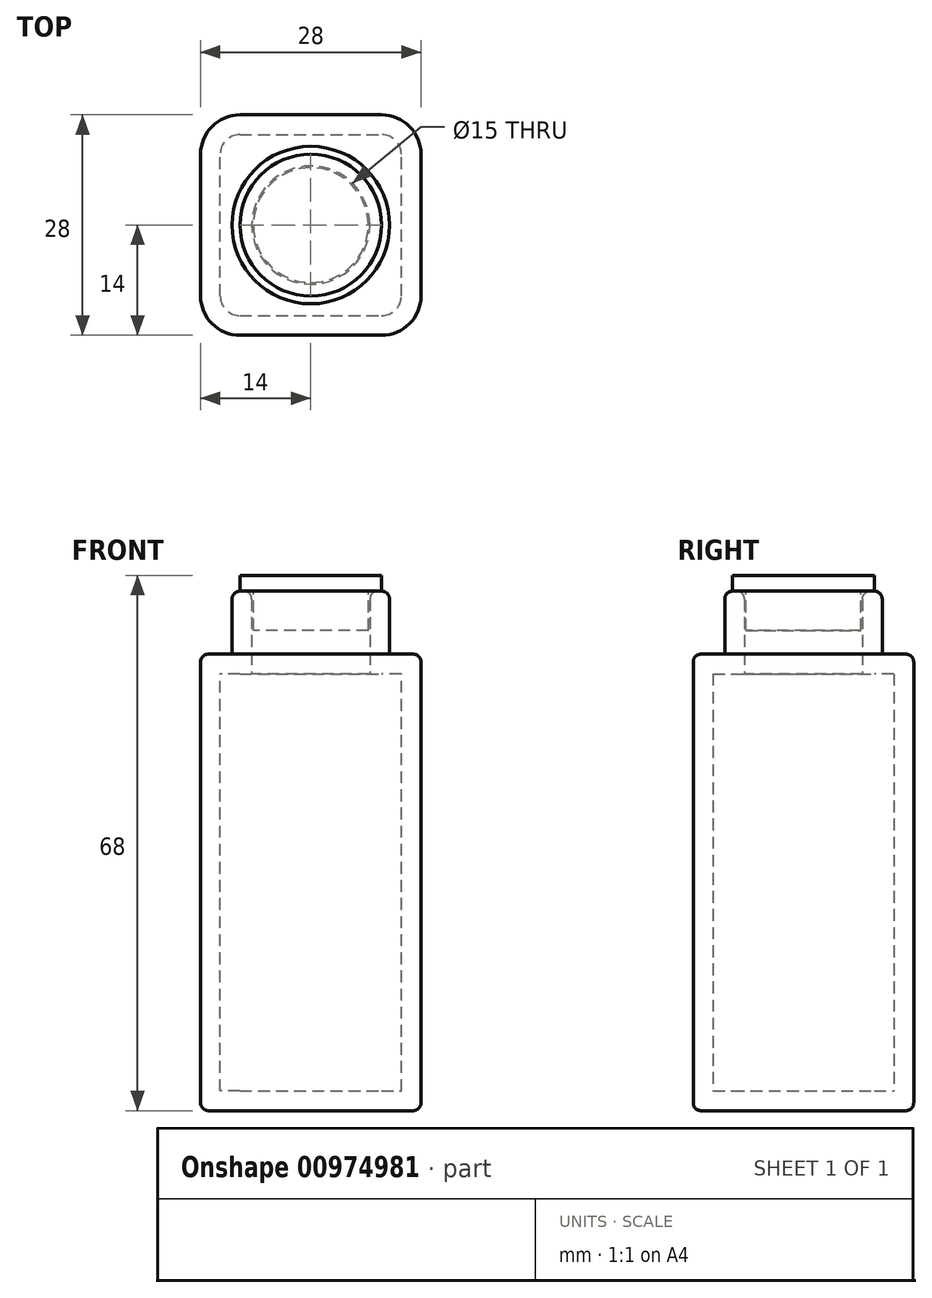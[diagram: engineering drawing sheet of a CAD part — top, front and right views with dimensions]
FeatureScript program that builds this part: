
annotation { "Feature Type Name" : "Feature", "Feature Type Description" : "" }
export const myFeature = defineFeature(function(context is Context, id is Id, definition is map)
    precondition{}
    {
        {
            var Q0;
            Q0=qCreatedBy(makeId("Top.planeOp"),FACE);
            var sketch = newSketch(context, id + "F0", { "sketchPlane" : qUnion([Q0])});
            skLineSegment(sketch, "E0.bottom", {"start": v(14, -14) * mm, "end": v(-14, -14) * mm});
            skLineSegment(sketch, "E0.top", {"start": v(14, 14) * mm, "end": v(-14, 14) * mm});
            skLineSegment(sketch, "E0.left", {"start": v(14, -14) * mm, "end": v(14, 14) * mm});
            skLineSegment(sketch, "E0.right", {"start": v(-14, -14) * mm, "end": v(-14, 14) * mm});
            skPoint(sketch, "E0.middle", {"position": v(0, 0) * mm});
            skSolve(sketch);
        }
        {
            var Q0;
            Q0=makeQuery(id+"F0.imprint","IMPRINT",FACE,{"disambiguationData":[TD([[makeQuery(id+"F0.imprint","IMPRINT",EDGE,{"derivedFrom":sQuery(id+"F0.wireOp",EDGE,"E0.bottom")}),-1.0]])]});
            extrude(context, id + "F1", {"entities" : qUnion([Q0]), "depth" : 58 * mm, "offsetDistance" : 25 * mm});
        }
        {
            var Q0;
            Q0=makeQuery(id+"F1.opExtrude","CAP_FACE",FACE,{"disambiguationData":[OSD([sQuery(id+"F0.wireOp",EDGE,"E0.bottom"),sQuery(id+"F0.wireOp",EDGE,"E0.top"),sQuery(id+"F0.wireOp",EDGE,"E0.left"),sQuery(id+"F0.wireOp",EDGE,"E0.right")])],"isStart":false});
            var sketch = newSketch(context, id + "F2", { "sketchPlane" : qUnion([Q0])});
            skCircle(sketch, "E1", {"center": v(0, 0) * mm, "radius": 10 * mm});
            skSolve(sketch);
        }
        {
            var Q0;
            Q0=makeQuery(id+"F2.imprint","IMPRINT",FACE,{"disambiguationData":[TD([[makeQuery(id+"F2.imprint","IMPRINT",EDGE,{"derivedFrom":sQuery(id+"F2.wireOp",EDGE,"E1")}),1.0]])]});
            extrude(context, id + "F3", {"entities" : qUnion([Q0]), "operationType" : NewBodyOperationType.ADD, "depth" : 8 * mm, "offsetDistance" : 25 * mm});
        }
        {
            var Q0;
            Q0=makeQuery(id+"F1.opExtrude","SWEPT_EDGE",EDGE,{"disambiguationData":[OSD([sQuery(id+"F0.wireOp",EDGE,"E0.bottom"),sQuery(id+"F0.wireOp",EDGE,"E0.right")])]});
            var Q1;
            Q1=makeQuery(id+"F1.opExtrude","SWEPT_EDGE",EDGE,{"disambiguationData":[OSD([sQuery(id+"F0.wireOp",EDGE,"E0.bottom"),sQuery(id+"F0.wireOp",EDGE,"E0.left")])]});
            var Q2;
            Q2=makeQuery(id+"F1.opExtrude","SWEPT_EDGE",EDGE,{"disambiguationData":[OSD([sQuery(id+"F0.wireOp",EDGE,"E0.top"),sQuery(id+"F0.wireOp",EDGE,"E0.left")])]});
            var Q3;
            Q3=makeQuery(id+"F1.opExtrude","SWEPT_EDGE",EDGE,{"disambiguationData":[OSD([sQuery(id+"F0.wireOp",EDGE,"E0.top"),sQuery(id+"F0.wireOp",EDGE,"E0.right")])]});
            fillet(context, id + "F4", {"entities" : qUnion([Q0, Q1, Q2, Q3]), "radius" : 5 * mm, "tangentPropagation" : true, "allowEdgeOverflow" : false});
        }
        {
            var Q0;
            Q0=makeQuery(id+"F3.opExtrude","CAP_EDGE",EDGE,{"disambiguationData":[OSD([sQuery(id+"F2.wireOp",EDGE,"E1")])],"isStart":true});
            var Q1;
            Q1=makeQuery(id+"F1.opExtrude","CAP_EDGE",EDGE,{"disambiguationData":[OSD([sQuery(id+"F0.wireOp",EDGE,"E0.right")])],"isStart":false});
            var Q2;
            Q2=makeQuery(id+"F1.opExtrude","CAP_EDGE",EDGE,{"disambiguationData":[OSD([sQuery(id+"F0.wireOp",EDGE,"E0.right")])],"isStart":true});
            fillet(context, id + "F5", {"entities" : qUnion([Q0, Q1, Q2]), "radius" : 1 * mm, "tangentPropagation" : true, "allowEdgeOverflow" : false});
        }
        {
            var Q0;
            Q0=makeQuery(id+"F3.opExtrude","CAP_FACE",FACE,{"disambiguationData":[OSD([sQuery(id+"F2.wireOp",EDGE,"E1")])],"isStart":false});
            shell(context, id + "F6", {"entities" : qUnion([Q0]), "thickness" : 2.5 * mm});
        }
        {
            var Q0;
            Q0=makeQuery(id+"F3.opExtrude","CAP_EDGE",EDGE,{"disambiguationData":[OSD([sQuery(id+"F2.wireOp",EDGE,"E1")])],"isStart":false});
            var Q1;
            {var subQ0=sQuery(id+"F2.wireOp",EDGE,"E1");Q1=makeQuery(id+"F6.opShell","OFFSET_EDGE",EDGE,{"disambiguationData":[OSD([subQ0]),TDD([makeQuery(id+"F3.opExtrude","CAP_EDGE",EDGE,{"disambiguationData":[OSD([subQ0])],"isStart":false})])]});}
            fillet(context, id + "F7", {"entities" : qUnion([Q0, Q1]), "radius" : 1 * mm, "tangentPropagation" : true, "allowEdgeOverflow" : false});
        }
        {
            var Q0;
            Q0=qCreatedBy(makeId("Front.planeOp"),FACE);
            var sketch = newSketch(context, id + "F8", { "sketchPlane" : qUnion([Q0])});
            skLineSegment(sketch, "E2", {"start": v(0, 68) * mm, "end": v(0, 61) * mm});
            skLineSegment(sketch, "E3", {"start": v(0, 61) * mm, "end": v(7.3, 61) * mm});
            skLineSegment(sketch, "E4", {"start": v(7.3, 61) * mm, "end": v(7.3, 66) * mm});
            skLineSegment(sketch, "E5", {"start": v(7.3, 66) * mm, "end": v(9, 66) * mm});
            skLineSegment(sketch, "E6", {"start": v(9, 66) * mm, "end": v(9, 68) * mm});
            skLineSegment(sketch, "E7", {"start": v(9, 68) * mm, "end": v(0, 68) * mm});
            skLineSegment(sketch, "E8", {"start": v(-7.5, 59) * mm, "end": v(-7.5, 65) * mm});
            skLineSegment(sketch, "E9", {"start": v(7.5, 65) * mm, "end": v(7.5, 59) * mm});
            skLineSegment(sketch, "E10", {"start": v(7.5, 65) * mm, "end": v(7.5, 59) * mm, "construction": true});
            skSolve(sketch);
        }
        {
            var Q0;
            Q0=makeQuery(id+"F8.imprint","IMPRINT",FACE,{"disambiguationData":[TD([[makeQuery(id+"F8.imprint","IMPRINT",EDGE,{"derivedFrom":sQuery(id+"F8.wireOp",EDGE,"E2")}),1.0]])]});
            var Q1;
            Q1=sQuery(id+"F8.wireOp",EDGE,"E2");
            revolve(context, id + "F9", {"surfaceOperationType" : NewSurfaceOperationType.NEW, "entities" : qUnion([Q0]), "axis" : qUnion([Q1]), "revolveType" : RevolveType.FULL});
        }
    });
